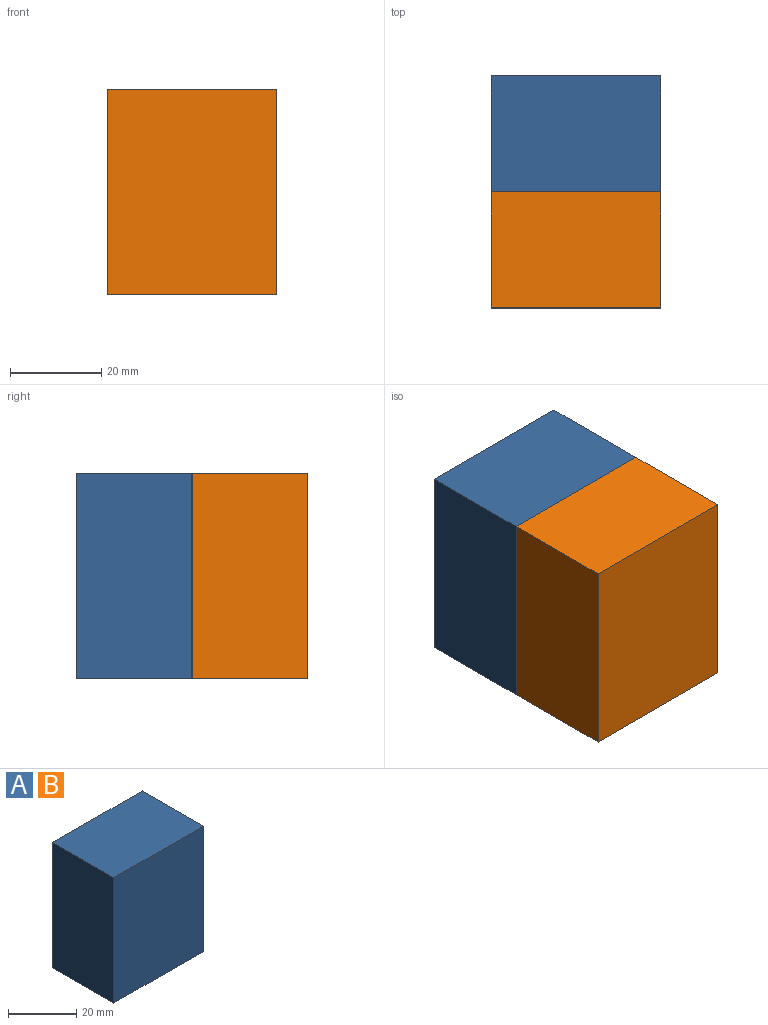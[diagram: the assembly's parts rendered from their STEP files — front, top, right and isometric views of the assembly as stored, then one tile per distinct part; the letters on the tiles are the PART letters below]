
ASSEMBLY  parts=2 mates=1
PART A: 6 faces, bbox 37.1x25.4x45.1 mm
  f0: plane 37.11x25.4mm, normal (0,0,1), area 942.5mm2, adj f1,f3,f4,f5
  f1: plane 45.11x25.4mm, normal (-1,0,0), area 1145.8mm2, adj f0,f2,f4,f5
  f2: plane 37.11x25.4mm, normal (0,0,-1), area 942.5mm2, adj f1,f3,f4,f5
  f3: plane 45.11x25.4mm, normal (1,0,0), area 1145.8mm2, adj f0,f2,f4,f5
  f4: plane 45.11x37.11mm, normal (0,-1,0), area 1673.9mm2, adj f0,f1,f2,f3
  f5: plane 45.11x37.11mm, normal (0,1,0), area 1673.9mm2, adj f0,f1,f2,f3
PART B: same geometry as A
PLACE A t=(9.21,-0.42,-8.61)mm
PLACE B rot(axis=(1,0,0),180deg) t=(9.21,-51.22,36.5)mm
MATE fastened B.f4 <-> A.f4  axis (0,1,0) through (58.92,-25.82,13.95)mm
